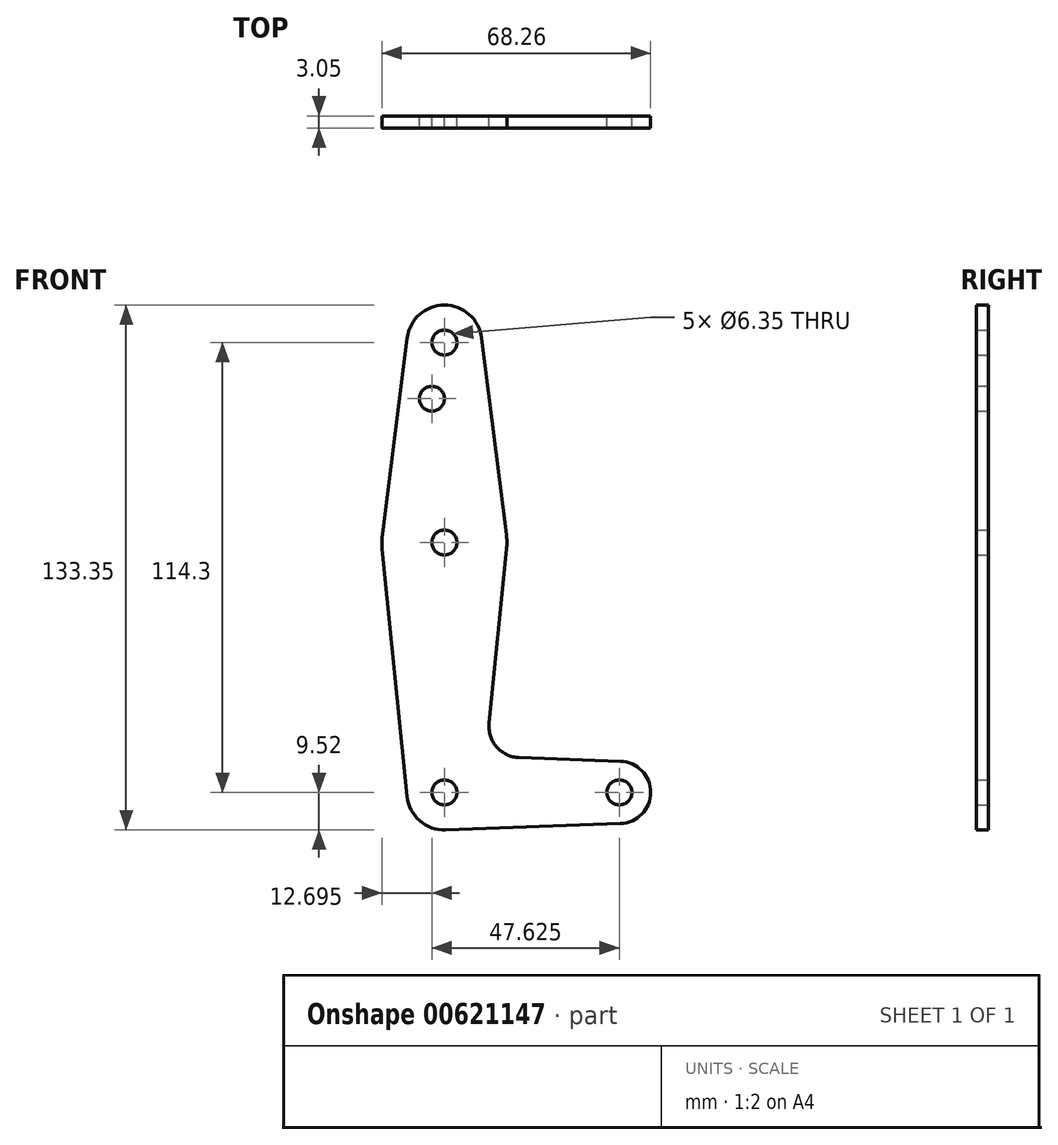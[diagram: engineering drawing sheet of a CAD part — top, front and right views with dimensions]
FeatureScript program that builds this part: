
annotation { "Feature Type Name" : "Feature", "Feature Type Description" : "" }
export const myFeature = defineFeature(function(context is Context, id is Id, definition is map)
    precondition{}
    {
        {
            var Q0;
            Q0=qCreatedBy(makeId("Front.planeOp"),FACE);
            var sketch = newSketch(context, id + "F0", { "sketchPlane" : qUnion([Q0])});
            skLineSegment(sketch, "E0", {"start": v(0, 0) * mm, "end": v(0, 114.3) * mm, "construction": true});
            skLineSegment(sketch, "E1", {"start": v(0, 0) * mm, "end": v(44.45, 0) * mm, "construction": true});
            skCircle(sketch, "E2", {"center": v(0, 0) * mm, "radius": 9.53 * mm});
            skCircle(sketch, "E3", {"center": v(44.45, 0) * mm, "radius": 7.94 * mm});
            skCircle(sketch, "E4", {"center": v(0, 114.3) * mm, "radius": 9.53 * mm});
            skCircle(sketch, "E5", {"center": v(0, 63.5) * mm, "radius": 15.88 * mm});
            skLineSegment(sketch, "E6", {"start": v(-9.45, 115.5) * mm, "end": v(-15.75, 65.48) * mm});
            skLineSegment(sketch, "E7", {"start": v(-15.8, 61.91) * mm, "end": v(-9.48, -0.95) * mm});
            skLineSegment(sketch, "E8", {"start": v(44.73, -7.93) * mm, "end": v(0.34, -9.52) * mm});
            skLineSegment(sketch, "E9.MirrorCS", {"start": v(9.45, 115.5) * mm, "end": v(15.75, 65.48) * mm});
            skLineSegment(sketch, "E10.MirrorCS", {"start": v(15.8, 61.91) * mm, "end": v(11.34, 17.6) * mm});
            skLineSegment(sketch, "E11.MirrorCS", {"start": v(44.73, 7.93) * mm, "end": v(18.97, 8.85) * mm});
            skCircle(sketch, "E12", {"center": v(0, 114.3) * mm, "radius": 3.18 * mm});
            skCircle(sketch, "E13", {"center": v(0, 63.5) * mm, "radius": 3.18 * mm});
            skCircle(sketch, "E14", {"center": v(0, 0) * mm, "radius": 3.18 * mm});
            skCircle(sketch, "E15", {"center": v(44.45, 0) * mm, "radius": 3.18 * mm});
            skCircle(sketch, "E16", {"center": v(-3.18, 100.03) * mm, "radius": 3.18 * mm});
            skPoint(sketch, "E17.newPointA", {"position": v(0.34, 9.52) * mm});
            skPoint(sketch, "E17.newPointB", {"position": v(9.48, -0.95) * mm});
            skArc(sketch, "E17.filletArc", {"start": v(11.34, 17.6) * mm, "mid": v(13.26, 11.57) * mm, "end": v(18.97, 8.85) * mm});
            skSolve(sketch);
        }
        {
            var Q0;
            Q0=makeQuery(id+"F0.imprint","IMPRINT",FACE,{"disambiguationData":[TD([[makeQuery(id+"F0.imprint","IMPRINT",EDGE,{"derivedFrom":sQuery(id+"F0.wireOp",EDGE,"E12")}),-1.0]])]});
            var Q1;
            {var subQ1=sQuery(id+"F0.wireOp",EDGE,"E6");Q1=makeQuery(id+"F0.imprint","IMPRINT",FACE,{"disambiguationData":[TD([[makeQuery(id+"F0.imprint","IMPRINT",EDGE,{"derivedFrom":subQ1}),1.0]])]});}
            var Q2;
            Q2=makeQuery(id+"F0.imprint","IMPRINT",FACE,{"disambiguationData":[TD([[makeQuery(id+"F0.imprint","IMPRINT",EDGE,{"derivedFrom":sQuery(id+"F0.wireOp",EDGE,"E13")}),-1.0]])]});
            var Q3;
            {var subQ0=sQuery(id+"F0.wireOp",EDGE,"E7");Q3=makeQuery(id+"F0.imprint","IMPRINT",FACE,{"disambiguationData":[TD([[makeQuery(id+"F0.imprint","IMPRINT",EDGE,{"derivedFrom":subQ0}),1.0]])]});}
            var Q4;
            Q4=makeQuery(id+"F0.imprint","IMPRINT",FACE,{"disambiguationData":[TD([[makeQuery(id+"F0.imprint","IMPRINT",EDGE,{"derivedFrom":sQuery(id+"F0.wireOp",EDGE,"E14")}),-1.0]])]});
            var Q5;
            Q5=makeQuery(id+"F0.imprint","IMPRINT",FACE,{"disambiguationData":[TD([[makeQuery(id+"F0.imprint","IMPRINT",EDGE,{"derivedFrom":sQuery(id+"F0.wireOp",EDGE,"E15")}),-1.0]])]});
            extrude(context, id + "F1", {"entities" : qUnion([Q0, Q1, Q2, Q3, Q4, Q5]), "depth" : 3.05 * mm, "offsetDistance" : 25.4 * mm});
        }
    });
